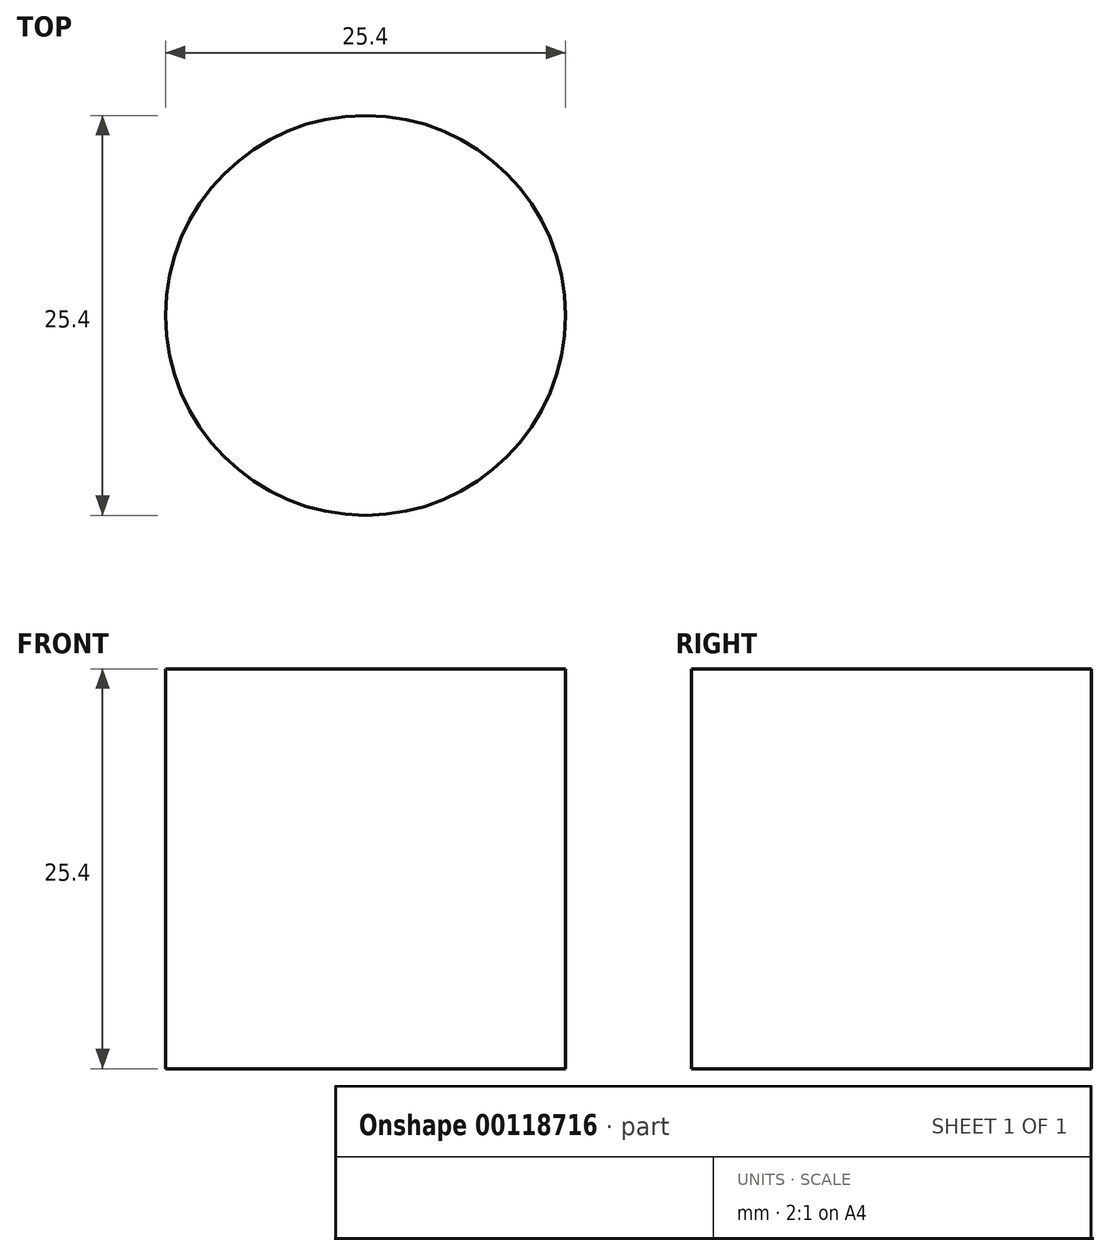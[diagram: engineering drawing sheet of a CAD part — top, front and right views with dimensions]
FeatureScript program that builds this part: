
annotation { "Feature Type Name" : "Feature", "Feature Type Description" : "" }
export const myFeature = defineFeature(function(context is Context, id is Id, definition is map)
    precondition{}
    {
        {
            var Q0;
            Q0=qCreatedBy(makeId("Top.planeOp"),FACE);
            var sketch = newSketch(context, id + "F0", { "sketchPlane" : qUnion([Q0])});
            skCircle(sketch, "E0", {"center": v(0, 0) * mm, "radius": 12.7 * mm});
            skSolve(sketch);
        }
        {
            var Q0;
            Q0=sQuery(id+"F0.wireOp",EDGE,"E0");
            extrude(context, id + "F1", {"bodyType" : ToolBodyType.SURFACE, "surfaceEntities" : qUnion([Q0]), "depth" : 25.4 * mm});
        }
    });
